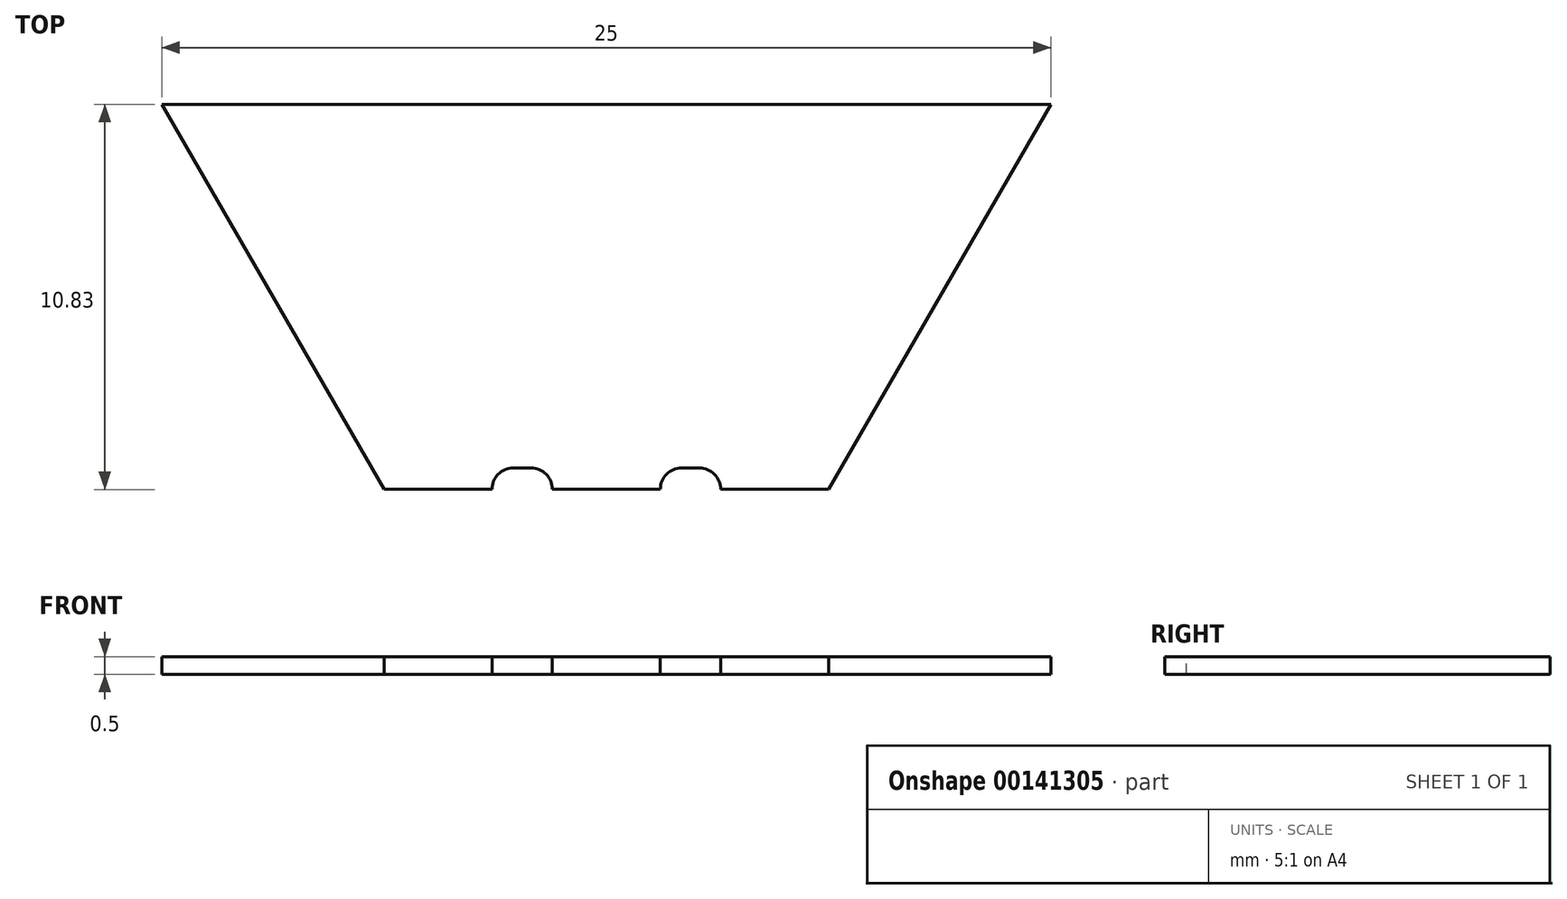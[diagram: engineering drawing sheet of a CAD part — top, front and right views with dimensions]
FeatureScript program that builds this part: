
annotation { "Feature Type Name" : "Feature", "Feature Type Description" : "" }
export const myFeature = defineFeature(function(context is Context, id is Id, definition is map)
    precondition{}
    {
        {
            var Q0;
            Q0=qCreatedBy(makeId("Top.planeOp"),FACE);
            var sketch = newSketch(context, id + "F0", { "sketchPlane" : qUnion([Q0])});
            skCircle(sketch, "E0.cCircle", {"center": v(0, 0) * mm, "radius": 12.5 * mm, "construction": true});
            skLineSegment(sketch, "E0.0", {"start": v(12.5, 0) * mm, "end": v(6.25, -10.83) * mm});
            skLineSegment(sketch, "E0.1", {"start": v(6.25, -10.83) * mm, "end": v(-6.25, -10.83) * mm});
            skLineSegment(sketch, "E0.2", {"start": v(-6.25, -10.83) * mm, "end": v(-12.5, 0) * mm});
            skLineSegment(sketch, "E0.3", {"start": v(-12.5, 0) * mm, "end": v(-6.25, 10.83) * mm});
            skLineSegment(sketch, "E0.4", {"start": v(-6.25, 10.83) * mm, "end": v(6.25, 10.83) * mm});
            skLineSegment(sketch, "E0.5", {"start": v(6.25, 10.83) * mm, "end": v(12.5, 0) * mm});
            skSolve(sketch);
        }
        {
            var Q0;
            Q0=qSketchRegion(id+"F0",true);
            extrude(context, id + "F1", {"entities" : qUnion([Q0]), "depth" : 0.5 * mm});
        }
        {
            var Q0;
            Q0=makeQuery(id+"F1.opExtrude","CAP_FACE",FACE,{"disambiguationData":[OSD([sQuery(id+"F0.wireOp",EDGE,"E0.0"),sQuery(id+"F0.wireOp",EDGE,"E0.1"),sQuery(id+"F0.wireOp",EDGE,"E0.2"),sQuery(id+"F0.wireOp",EDGE,"E0.3"),sQuery(id+"F0.wireOp",EDGE,"E0.4"),sQuery(id+"F0.wireOp",EDGE,"E0.5")])],"isStart":false});
            var sketch = newSketch(context, id + "F2", { "sketchPlane" : qUnion([Q0])});
            skLineSegment(sketch, "E1", {"start": v(2.62, -10.23) * mm, "end": v(2.12, -10.23) * mm});
            skArc(sketch, "E2", {"start": v(2.12, -10.23) * mm, "mid": v(1.7, -10.4) * mm, "end": v(1.52, -10.83) * mm});
            skArc(sketch, "E3", {"start": v(3.22, -10.83) * mm, "mid": v(3.04, -10.4) * mm, "end": v(2.62, -10.23) * mm});
            skLineSegment(sketch, "E4", {"start": v(1.52, -10.83) * mm, "end": v(3.22, -10.83) * mm});
            skLineSegment(sketch, "E5.MirrorCS", {"start": v(-1.52, -10.83) * mm, "end": v(-3.22, -10.83) * mm});
            skArc(sketch, "E6.MirrorCS", {"start": v(-3.22, -10.83) * mm, "mid": v(-3.04, -10.4) * mm, "end": v(-2.62, -10.23) * mm});
            skArc(sketch, "E7.MirrorCS", {"start": v(-2.12, -10.23) * mm, "mid": v(-1.7, -10.4) * mm, "end": v(-1.52, -10.83) * mm});
            skLineSegment(sketch, "E8.MirrorCS", {"start": v(-2.62, -10.23) * mm, "end": v(-2.12, -10.23) * mm});
            skLineSegment(sketch, "E9", {"start": v(-6.25, -10.83) * mm, "end": v(-3.22, -10.83) * mm, "construction": true});
            skLineSegment(sketch, "E10", {"start": v(-1.52, -10.83) * mm, "end": v(1.52, -10.83) * mm, "construction": true});
            skLineSegment(sketch, "E11", {"start": v(3.22, -10.83) * mm, "end": v(6.25, -10.83) * mm, "construction": true});
            skSolve(sketch);
        }
        {
            var Q0;
            Q0=qSketchRegion(id+"F2",true);
            extrude(context, id + "F3", {"entities" : qUnion([Q0]), "operationType" : NewBodyOperationType.REMOVE, "endBound" : BoundingType.THROUGH_ALL, "oppositeDirection" : true, "depth" : 25 * mm});
        }
        {
            var Q0;
            Q0=makeQuery(id+"F1.opExtrude","CAP_FACE",FACE,{"disambiguationData":[OSD([sQuery(id+"F0.wireOp",EDGE,"E0.0"),sQuery(id+"F0.wireOp",EDGE,"E0.1"),sQuery(id+"F0.wireOp",EDGE,"E0.2"),sQuery(id+"F0.wireOp",EDGE,"E0.3"),sQuery(id+"F0.wireOp",EDGE,"E0.4"),sQuery(id+"F0.wireOp",EDGE,"E0.5")])],"isStart":false});
            var sketch = newSketch(context, id + "F4", { "sketchPlane" : qUnion([Q0])});
            skLineSegment(sketch, "E12", {"start": v(-12.5, 0) * mm, "end": v(12.5, 0) * mm});
            skLineSegment(sketch, "E13", {"start": v(12.5, 0) * mm, "end": v(6.25, 10.83) * mm});
            skLineSegment(sketch, "E14", {"start": v(6.25, 10.83) * mm, "end": v(-6.25, 10.83) * mm});
            skLineSegment(sketch, "E15", {"start": v(-6.25, 10.83) * mm, "end": v(-12.5, 0) * mm});
            skSolve(sketch);
        }
        {
            var Q0;
            Q0 = qSketchRegion(id + "F4", true);
            extrude(context, id + "F5", {"entities" : qUnion([Q0]), "operationType" : NewBodyOperationType.REMOVE, "endBound" : BoundingType.THROUGH_ALL, "oppositeDirection" : true, "depth" : 25 * mm});
        }
    });
